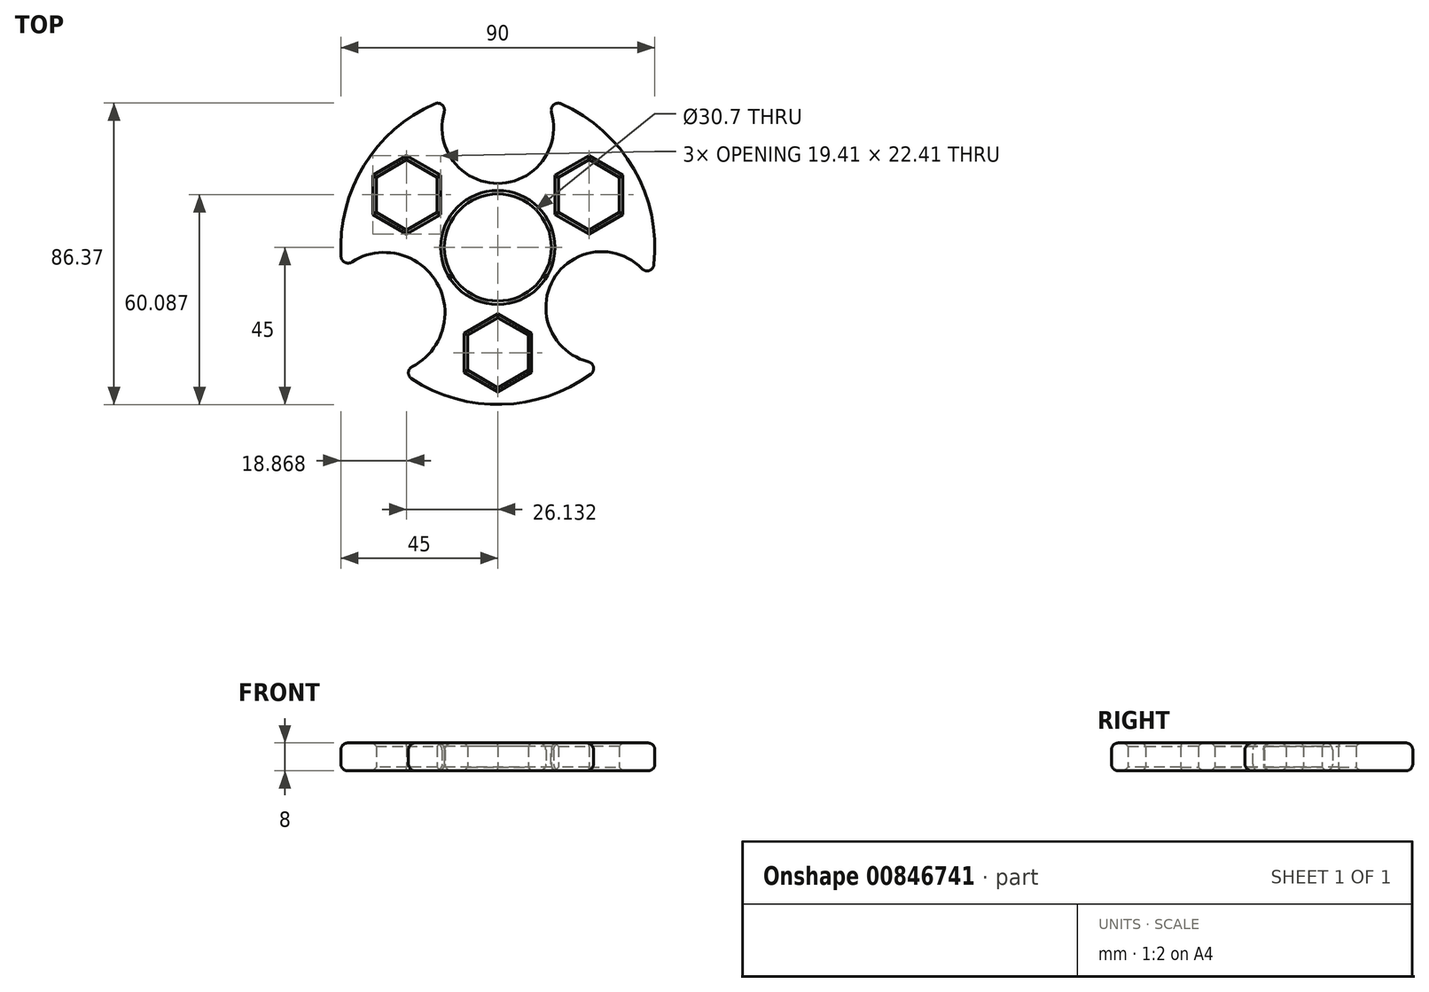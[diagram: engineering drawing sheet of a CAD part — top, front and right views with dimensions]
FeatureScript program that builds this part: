
annotation { "Feature Type Name" : "Feature", "Feature Type Description" : "" }
export const myFeature = defineFeature(function(context is Context, id is Id, definition is map)
    precondition{}
    {
        {
            var Q0;
            Q0=qCreatedBy(makeId("Top.planeOp"),FACE);
            var sketch = newSketch(context, id + "F0", { "sketchPlane" : qUnion([Q0])});
            skCircle(sketch, "E0", {"center": v(0, 0) * mm, "radius": 15.35 * mm});
            skPoint(sketch, "E1", {"position": v(-17.47, -10.09) * mm});
            skPoint(sketch, "E2", {"position": v(0, 15.35) * mm});
            skPoint(sketch, "E3", {"position": v(17.47, -10.09) * mm});
            skPoint(sketch, "E4", {"position": v(0, 20.18) * mm});
            skArc(sketch, "E5", {"start": v(-27.76, -35.42) * mm, "mid": v(-17.47, -10.09) * mm, "end": v(-44.55, -6.33) * mm});
            skArc(sketch, "E6", {"start": v(-13.53, 42.92) * mm, "mid": v(-38.07, 23.99) * mm, "end": v(-44.55, -6.33) * mm});
            skCircle(sketch, "E7.cCircle", {"center": v(-26.13, 15.09) * mm, "radius": 10.05 * mm, "construction": true});
            skLineSegment(sketch, "E7.0", {"start": v(-17.43, 10.06) * mm, "end": v(-26.13, 5.04) * mm});
            skLineSegment(sketch, "E7.1", {"start": v(-26.13, 5.04) * mm, "end": v(-34.84, 10.06) * mm});
            skLineSegment(sketch, "E7.2", {"start": v(-34.84, 10.06) * mm, "end": v(-34.84, 20.11) * mm});
            skLineSegment(sketch, "E7.3", {"start": v(-34.84, 20.11) * mm, "end": v(-26.13, 25.14) * mm});
            skLineSegment(sketch, "E7.4", {"start": v(-26.13, 25.14) * mm, "end": v(-17.43, 20.11) * mm});
            skLineSegment(sketch, "E7.5", {"start": v(-17.43, 20.11) * mm, "end": v(-17.43, 10.06) * mm});
            skArc(sketch, "E8", {"start": v(-13.53, 42.92) * mm, "mid": v(0, 18.38) * mm, "end": v(13.53, 42.92) * mm});
            skArc(sketch, "E9", {"start": v(43.93, -9.74) * mm, "mid": v(15.91, -9.19) * mm, "end": v(30.4, -33.17) * mm});
            skPoint(sketch, "E10.orphan", {"position": v(-43.3, 25) * mm});
            skCircle(sketch, "E11.cCircle", {"center": v(26.13, 15.09) * mm, "radius": 10.05 * mm, "construction": true});
            skLineSegment(sketch, "E11.0", {"start": v(17.43, 10.06) * mm, "end": v(17.43, 20.11) * mm});
            skLineSegment(sketch, "E11.1", {"start": v(17.43, 20.11) * mm, "end": v(26.13, 25.14) * mm});
            skLineSegment(sketch, "E11.2", {"start": v(26.13, 25.14) * mm, "end": v(34.84, 20.11) * mm});
            skLineSegment(sketch, "E11.3", {"start": v(34.84, 20.11) * mm, "end": v(34.84, 10.06) * mm});
            skLineSegment(sketch, "E11.4", {"start": v(34.84, 10.06) * mm, "end": v(26.13, 5.04) * mm});
            skLineSegment(sketch, "E11.5", {"start": v(26.13, 5.04) * mm, "end": v(17.43, 10.06) * mm});
            skCircle(sketch, "E12.cCircle", {"center": v(0, -30.18) * mm, "radius": 10.05 * mm, "construction": true});
            skLineSegment(sketch, "E12.0", {"start": v(0, -20.12) * mm, "end": v(8.7, -25.15) * mm});
            skLineSegment(sketch, "E12.1", {"start": v(8.7, -25.15) * mm, "end": v(8.7, -35.2) * mm});
            skLineSegment(sketch, "E12.2", {"start": v(8.7, -35.2) * mm, "end": v(0, -40.23) * mm});
            skLineSegment(sketch, "E12.3", {"start": v(0, -40.23) * mm, "end": v(-8.7, -35.2) * mm});
            skLineSegment(sketch, "E12.4", {"start": v(-8.7, -35.2) * mm, "end": v(-8.7, -25.15) * mm});
            skLineSegment(sketch, "E12.5", {"start": v(-8.7, -25.15) * mm, "end": v(0, -20.12) * mm});
            skPoint(sketch, "E13.start.orphan", {"position": v(0, 50) * mm});
            skPoint(sketch, "E14.trimOffspring.end.orphan", {"position": v(0, 25) * mm});
            skPoint(sketch, "E14.trimOffspring.start.orphan", {"position": v(0, 31.25) * mm});
            skPoint(sketch, "E15.end.orphan", {"position": v(0, 37.5) * mm});
            skPoint(sketch, "E16.orphan", {"position": v(0, -50) * mm});
            skArc(sketch, "E17.trimOffspring", {"start": v(43.93, -9.74) * mm, "mid": v(38.97, 22.5) * mm, "end": v(13.53, 42.92) * mm});
            skPoint(sketch, "E18.start.orphan", {"position": v(43.3, -25) * mm});
            skPoint(sketch, "E19.orphan", {"position": v(32.48, -18.75) * mm});
            skPoint(sketch, "E20.start.orphan", {"position": v(21.65, -12.5) * mm});
            skPoint(sketch, "E21.start.orphan", {"position": v(27.06, -15.62) * mm});
            skArc(sketch, "E22.trimOffspring", {"start": v(-27.76, -35.42) * mm, "mid": v(1.74, -44.97) * mm, "end": v(30.4, -33.17) * mm});
            skPoint(sketch, "E23.orphan", {"position": v(-43.3, -25) * mm});
            skPoint(sketch, "E24.end.orphan", {"position": v(-21.65, -12.5) * mm});
            skPoint(sketch, "E25.end.orphan", {"position": v(-13.3, -7.67) * mm});
            skPoint(sketch, "E26.start.orphan", {"position": v(0, -15.35) * mm});
            skPoint(sketch, "E27.start.orphan", {"position": v(0, -45) * mm});
            skPoint(sketch, "E28.orphan", {"position": v(-38.97, 22.5) * mm});
            skPoint(sketch, "E29.orphan", {"position": v(-28.3, 16.34) * mm});
            skPoint(sketch, "E30.start.orphan", {"position": v(-13.3, 7.67) * mm});
            skPoint(sketch, "E31.orphan", {"position": v(13.3, 7.68) * mm});
            skPoint(sketch, "E32.start.orphan", {"position": v(38.97, 22.5) * mm});
            skSolve(sketch);
        }
        {
            var Q0;
            Q0 = qSketchRegion(id + "F0", true);
            extrude(context, id + "F1", {"entities" : qUnion([Q0]), "depth" : 8 * mm, "offsetDistance" : 25 * mm});
        }
        {
            var Q0;
            Q0=makeQuery(id+"F1.opExtrude","CAP_EDGE",EDGE,{"disambiguationData":[OSD([sQuery(id+"F0.wireOp",EDGE,"E8")])],"isStart":false});
            var Q1;
            Q1=makeQuery(id+"F1.opExtrude","CAP_EDGE",EDGE,{"disambiguationData":[OSD([sQuery(id+"F0.wireOp",EDGE,"E8")])],"isStart":true});
            var Q2;
            Q2=makeQuery(id+"F1.opExtrude","CAP_EDGE",EDGE,{"disambiguationData":[OSD([sQuery(id+"F0.wireOp",EDGE,"E6")])],"isStart":true});
            var Q3;
            Q3=makeQuery(id+"F1.opExtrude","CAP_EDGE",EDGE,{"disambiguationData":[OSD([sQuery(id+"F0.wireOp",EDGE,"E6")])],"isStart":false});
            var Q4;
            Q4=makeQuery(id+"F1.opExtrude","SWEPT_EDGE",EDGE,{"disambiguationData":[OSD([sQuery(id+"F0.wireOp",EDGE,"E6"),sQuery(id+"F0.wireOp",EDGE,"E8")])]});
            var Q5;
            Q5=makeQuery(id+"F1.opExtrude","SWEPT_EDGE",EDGE,{"disambiguationData":[OSD([sQuery(id+"F0.wireOp",EDGE,"E8"),sQuery(id+"F0.wireOp",EDGE,"E17.trimOffspring")])]});
            var Q6;
            Q6=makeQuery(id+"F1.opExtrude","CAP_EDGE",EDGE,{"disambiguationData":[OSD([sQuery(id+"F0.wireOp",EDGE,"E5")])],"isStart":false});
            var Q7;
            Q7=makeQuery(id+"F1.opExtrude","CAP_EDGE",EDGE,{"disambiguationData":[OSD([sQuery(id+"F0.wireOp",EDGE,"E5")])],"isStart":true});
            var Q8;
            Q8=makeQuery(id+"F1.opExtrude","CAP_EDGE",EDGE,{"disambiguationData":[OSD([sQuery(id+"F0.wireOp",EDGE,"E9")])],"isStart":false});
            var Q9;
            Q9=makeQuery(id+"F1.opExtrude","CAP_EDGE",EDGE,{"disambiguationData":[OSD([sQuery(id+"F0.wireOp",EDGE,"E9")])],"isStart":true});
            var Q10;
            Q10=makeQuery(id+"F1.opExtrude","CAP_EDGE",EDGE,{"disambiguationData":[OSD([sQuery(id+"F0.wireOp",EDGE,"E17.trimOffspring")])],"isStart":false});
            var Q11;
            Q11=makeQuery(id+"F1.opExtrude","CAP_EDGE",EDGE,{"disambiguationData":[OSD([sQuery(id+"F0.wireOp",EDGE,"E22.trimOffspring")])],"isStart":false});
            var Q12;
            Q12=makeQuery(id+"F1.opExtrude","SWEPT_EDGE",EDGE,{"disambiguationData":[OSD([sQuery(id+"F0.wireOp",EDGE,"E9"),sQuery(id+"F0.wireOp",EDGE,"E17.trimOffspring")])]});
            var Q13;
            Q13=makeQuery(id+"F1.opExtrude","SWEPT_EDGE",EDGE,{"disambiguationData":[OSD([sQuery(id+"F0.wireOp",EDGE,"E9"),sQuery(id+"F0.wireOp",EDGE,"E22.trimOffspring")])]});
            var Q14;
            Q14=makeQuery(id+"F1.opExtrude","SWEPT_EDGE",EDGE,{"disambiguationData":[OSD([sQuery(id+"F0.wireOp",EDGE,"E5"),sQuery(id+"F0.wireOp",EDGE,"E6")])]});
            var Q15;
            Q15=makeQuery(id+"F1.opExtrude","SWEPT_EDGE",EDGE,{"disambiguationData":[OSD([sQuery(id+"F0.wireOp",EDGE,"E5"),sQuery(id+"F0.wireOp",EDGE,"E22.trimOffspring")])]});
            var Q16;
            Q16=makeQuery(id+"F1.opExtrude","CAP_EDGE",EDGE,{"disambiguationData":[OSD([sQuery(id+"F0.wireOp",EDGE,"E22.trimOffspring")])],"isStart":true});
            var Q17;
            Q17=makeQuery(id+"F1.opExtrude","CAP_EDGE",EDGE,{"disambiguationData":[OSD([sQuery(id+"F0.wireOp",EDGE,"E17.trimOffspring")])],"isStart":true});
            fillet(context, id + "F2", {"entities" : qUnion([Q0, Q1, Q2, Q3, Q4, Q5, Q6, Q7, Q8, Q9, Q10, Q11, Q12, Q13, Q14, Q15, Q16, Q17]), "radius" : 2 * mm, "tangentPropagation" : true, "allowEdgeOverflow" : false});
        }
        {
            var Q0;
            Q0=makeQuery(id+"F1.opExtrude","CAP_EDGE",EDGE,{"disambiguationData":[OSD([sQuery(id+"F0.wireOp",EDGE,"E7.2")])],"isStart":true});
            var Q1;
            Q1=makeQuery(id+"F1.opExtrude","CAP_EDGE",EDGE,{"disambiguationData":[OSD([sQuery(id+"F0.wireOp",EDGE,"E7.3")])],"isStart":true});
            var Q2;
            Q2=makeQuery(id+"F1.opExtrude","CAP_EDGE",EDGE,{"disambiguationData":[OSD([sQuery(id+"F0.wireOp",EDGE,"E7.4")])],"isStart":true});
            var Q3;
            Q3=makeQuery(id+"F1.opExtrude","CAP_EDGE",EDGE,{"disambiguationData":[OSD([sQuery(id+"F0.wireOp",EDGE,"E7.5")])],"isStart":true});
            var Q4;
            Q4=makeQuery(id+"F1.opExtrude","CAP_EDGE",EDGE,{"disambiguationData":[OSD([sQuery(id+"F0.wireOp",EDGE,"E0")])],"isStart":true});
            var Q5;
            Q5=makeQuery(id+"F1.opExtrude","CAP_EDGE",EDGE,{"disambiguationData":[OSD([sQuery(id+"F0.wireOp",EDGE,"E0")])],"isStart":false});
            var Q6;
            Q6=makeQuery(id+"F1.opExtrude","CAP_EDGE",EDGE,{"disambiguationData":[OSD([sQuery(id+"F0.wireOp",EDGE,"E7.0")])],"isStart":true});
            var Q7;
            Q7=makeQuery(id+"F1.opExtrude","CAP_EDGE",EDGE,{"disambiguationData":[OSD([sQuery(id+"F0.wireOp",EDGE,"E7.1")])],"isStart":true});
            var Q8;
            Q8=makeQuery(id+"F1.opExtrude","CAP_EDGE",EDGE,{"disambiguationData":[OSD([sQuery(id+"F0.wireOp",EDGE,"E11.1")])],"isStart":true});
            var Q9;
            Q9=makeQuery(id+"F1.opExtrude","CAP_EDGE",EDGE,{"disambiguationData":[OSD([sQuery(id+"F0.wireOp",EDGE,"E11.0")])],"isStart":true});
            var Q10;
            Q10=makeQuery(id+"F1.opExtrude","CAP_EDGE",EDGE,{"disambiguationData":[OSD([sQuery(id+"F0.wireOp",EDGE,"E11.5")])],"isStart":true});
            var Q11;
            Q11=makeQuery(id+"F1.opExtrude","CAP_EDGE",EDGE,{"disambiguationData":[OSD([sQuery(id+"F0.wireOp",EDGE,"E11.4")])],"isStart":true});
            var Q12;
            Q12=makeQuery(id+"F1.opExtrude","CAP_EDGE",EDGE,{"disambiguationData":[OSD([sQuery(id+"F0.wireOp",EDGE,"E11.3")])],"isStart":true});
            var Q13;
            Q13=makeQuery(id+"F1.opExtrude","CAP_EDGE",EDGE,{"disambiguationData":[OSD([sQuery(id+"F0.wireOp",EDGE,"E11.3")])],"isStart":false});
            var Q14;
            Q14=makeQuery(id+"F1.opExtrude","CAP_EDGE",EDGE,{"disambiguationData":[OSD([sQuery(id+"F0.wireOp",EDGE,"E11.2")])],"isStart":false});
            var Q15;
            Q15=makeQuery(id+"F1.opExtrude","CAP_EDGE",EDGE,{"disambiguationData":[OSD([sQuery(id+"F0.wireOp",EDGE,"E11.2")])],"isStart":true});
            var Q16;
            Q16=makeQuery(id+"F1.opExtrude","CAP_EDGE",EDGE,{"disambiguationData":[OSD([sQuery(id+"F0.wireOp",EDGE,"E7.4")])],"isStart":false});
            var Q17;
            Q17=makeQuery(id+"F1.opExtrude","CAP_EDGE",EDGE,{"disambiguationData":[OSD([sQuery(id+"F0.wireOp",EDGE,"E7.5")])],"isStart":false});
            var Q18;
            Q18=makeQuery(id+"F1.opExtrude","CAP_EDGE",EDGE,{"disambiguationData":[OSD([sQuery(id+"F0.wireOp",EDGE,"E12.3")])],"isStart":true});
            var Q19;
            Q19=makeQuery(id+"F1.opExtrude","CAP_EDGE",EDGE,{"disambiguationData":[OSD([sQuery(id+"F0.wireOp",EDGE,"E12.2")])],"isStart":true});
            var Q20;
            Q20=makeQuery(id+"F1.opExtrude","CAP_EDGE",EDGE,{"disambiguationData":[OSD([sQuery(id+"F0.wireOp",EDGE,"E12.1")])],"isStart":true});
            var Q21;
            Q21=makeQuery(id+"F1.opExtrude","CAP_EDGE",EDGE,{"disambiguationData":[OSD([sQuery(id+"F0.wireOp",EDGE,"E12.1")])],"isStart":false});
            var Q22;
            Q22=makeQuery(id+"F1.opExtrude","CAP_EDGE",EDGE,{"disambiguationData":[OSD([sQuery(id+"F0.wireOp",EDGE,"E12.0")])],"isStart":false});
            var Q23;
            Q23=makeQuery(id+"F1.opExtrude","CAP_EDGE",EDGE,{"disambiguationData":[OSD([sQuery(id+"F0.wireOp",EDGE,"E12.0")])],"isStart":true});
            var Q24;
            Q24=makeQuery(id+"F1.opExtrude","CAP_EDGE",EDGE,{"disambiguationData":[OSD([sQuery(id+"F0.wireOp",EDGE,"E12.5")])],"isStart":true});
            var Q25;
            Q25=makeQuery(id+"F1.opExtrude","CAP_EDGE",EDGE,{"disambiguationData":[OSD([sQuery(id+"F0.wireOp",EDGE,"E12.4")])],"isStart":true});
            var Q26;
            Q26=makeQuery(id+"F1.opExtrude","CAP_EDGE",EDGE,{"disambiguationData":[OSD([sQuery(id+"F0.wireOp",EDGE,"E11.1")])],"isStart":false});
            var Q27;
            Q27=makeQuery(id+"F1.opExtrude","CAP_EDGE",EDGE,{"disambiguationData":[OSD([sQuery(id+"F0.wireOp",EDGE,"E11.0")])],"isStart":false});
            var Q28;
            Q28=makeQuery(id+"F1.opExtrude","CAP_EDGE",EDGE,{"disambiguationData":[OSD([sQuery(id+"F0.wireOp",EDGE,"E11.5")])],"isStart":false});
            var Q29;
            Q29=makeQuery(id+"F1.opExtrude","CAP_EDGE",EDGE,{"disambiguationData":[OSD([sQuery(id+"F0.wireOp",EDGE,"E11.4")])],"isStart":false});
            var Q30;
            Q30=makeQuery(id+"F1.opExtrude","CAP_EDGE",EDGE,{"disambiguationData":[OSD([sQuery(id+"F0.wireOp",EDGE,"E7.3")])],"isStart":false});
            var Q31;
            Q31=makeQuery(id+"F1.opExtrude","CAP_EDGE",EDGE,{"disambiguationData":[OSD([sQuery(id+"F0.wireOp",EDGE,"E7.2")])],"isStart":false});
            var Q32;
            Q32=makeQuery(id+"F1.opExtrude","CAP_EDGE",EDGE,{"disambiguationData":[OSD([sQuery(id+"F0.wireOp",EDGE,"E7.1")])],"isStart":false});
            var Q33;
            Q33=makeQuery(id+"F1.opExtrude","CAP_EDGE",EDGE,{"disambiguationData":[OSD([sQuery(id+"F0.wireOp",EDGE,"E7.0")])],"isStart":false});
            var Q34;
            Q34=makeQuery(id+"F1.opExtrude","CAP_EDGE",EDGE,{"disambiguationData":[OSD([sQuery(id+"F0.wireOp",EDGE,"E12.5")])],"isStart":false});
            var Q35;
            Q35=makeQuery(id+"F1.opExtrude","CAP_EDGE",EDGE,{"disambiguationData":[OSD([sQuery(id+"F0.wireOp",EDGE,"E12.4")])],"isStart":false});
            var Q36;
            Q36=makeQuery(id+"F1.opExtrude","CAP_EDGE",EDGE,{"disambiguationData":[OSD([sQuery(id+"F0.wireOp",EDGE,"E12.3")])],"isStart":false});
            var Q37;
            Q37=makeQuery(id+"F1.opExtrude","CAP_EDGE",EDGE,{"disambiguationData":[OSD([sQuery(id+"F0.wireOp",EDGE,"E12.2")])],"isStart":false});
            chamfer(context, id + "F3", {"entities" : qUnion([Q0, Q1, Q2, Q3, Q4, Q5, Q6, Q7, Q8, Q9, Q10, Q11, Q12, Q13, Q14, Q15, Q16, Q17, Q18, Q19, Q20, Q21, Q22, Q23, Q24, Q25, Q26, Q27, Q28, Q29, Q30, Q31, Q32, Q33, Q34, Q35, Q36, Q37]), "width" : 1 * mm, "tangentPropagation" : true});
        }
    });
